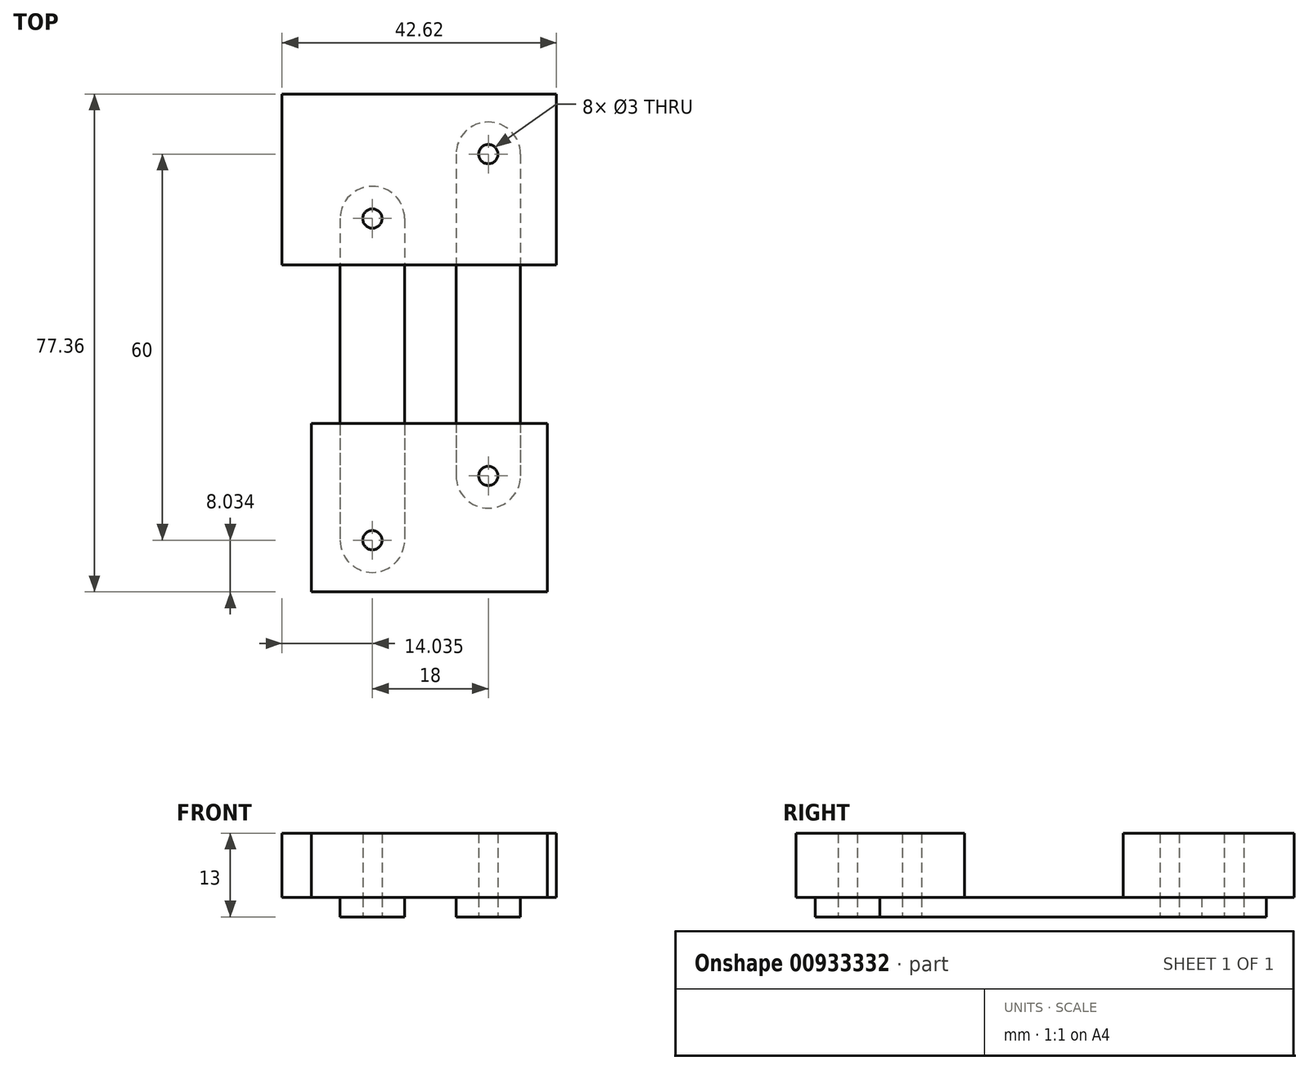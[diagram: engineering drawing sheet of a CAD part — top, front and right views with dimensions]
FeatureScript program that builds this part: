
annotation { "Feature Type Name" : "Feature", "Feature Type Description" : "" }
export const myFeature = defineFeature(function(context is Context, id is Id, definition is map)
    precondition{}
    {
        {
            var Q0;
            Q0=qCreatedBy(makeId("Top.planeOp"),FACE);
            var sketch = newSketch(context, id + "F0", { "sketchPlane" : qUnion([Q0])});
            skLineSegment(sketch, "E0.left", {"start": v(-39.37, 31.83) * mm, "end": v(-39.37, -18.17) * mm});
            skLineSegment(sketch, "E0.right", {"start": v(-29.37, 31.83) * mm, "end": v(-29.37, -18.17) * mm});
            skArc(sketch, "E1", {"start": v(-29.37, 31.83) * mm, "mid": v(-34.37, 36.83) * mm, "end": v(-39.37, 31.83) * mm});
            skArc(sketch, "E2", {"start": v(-39.37, -18.17) * mm, "mid": v(-34.37, -23.17) * mm, "end": v(-29.37, -18.17) * mm});
            skCircle(sketch, "E3", {"center": v(-34.37, 31.83) * mm, "radius": 1.5 * mm});
            skCircle(sketch, "E4", {"center": v(-34.37, -18.17) * mm, "radius": 1.5 * mm});
            skSolve(sketch);
        }
        {
            var Q0;
            Q0=makeQuery(id+"F0.imprint","IMPRINT",FACE,{"disambiguationData":[TD([[makeQuery(id+"F0.imprint","IMPRINT",EDGE,{"derivedFrom":sQuery(id+"F0.wireOp",EDGE,"E0.left")}),1.0]])]});
            extrude(context, id + "F1", {"entities" : qUnion([Q0]), "depth" : 3 * mm, "offsetDistance" : 25 * mm});
        }
        {
            var Q0;
            Q0=makeQuery(id+"F1.opExtrude","SWEPT_BODY",BODY,{"disambiguationData":[OSD([sQuery(id+"F0.wireOp",EDGE,"E0.left"),sQuery(id+"F0.wireOp",EDGE,"E0.right"),sQuery(id+"F0.wireOp",EDGE,"E1"),sQuery(id+"F0.wireOp",EDGE,"E2"),sQuery(id+"F0.wireOp",EDGE,"E3"),sQuery(id+"F0.wireOp",EDGE,"E4")])]});
            transform(context, id + "F2", {"entities" : qUnion([Q0]), "transformType" : TransformType.TRANSLATION_3D, "dx" : 18 * mm, "dy" : 10 * mm, "dz" : 0 * mm, "makeCopy" : true});
        }
        {
            var Q0;
            Q0=makeQuery(id+"F1.opExtrude","CAP_FACE",FACE,{"disambiguationData":[OSD([sQuery(id+"F0.wireOp",EDGE,"E0.left"),sQuery(id+"F0.wireOp",EDGE,"E0.right"),sQuery(id+"F0.wireOp",EDGE,"E1"),sQuery(id+"F0.wireOp",EDGE,"E2"),sQuery(id+"F0.wireOp",EDGE,"E3"),sQuery(id+"F0.wireOp",EDGE,"E4")])],"isStart":false});
            var sketch = newSketch(context, id + "F3", { "sketchPlane" : qUnion([Q0])});
            skLineSegment(sketch, "E5.bottom", {"start": v(-43.86, 0) * mm, "end": v(-7.2, 0) * mm});
            skLineSegment(sketch, "E5.top", {"start": v(-43.86, -26.2) * mm, "end": v(-7.2, -26.2) * mm});
            skLineSegment(sketch, "E5.left", {"start": v(-43.86, 0) * mm, "end": v(-43.86, -26.2) * mm});
            skLineSegment(sketch, "E5.right", {"start": v(-7.2, 0) * mm, "end": v(-7.2, -26.2) * mm});
            skCircle(sketch, "E6.0", {"center": v(-34.37, -18.17) * mm, "radius": 1.5 * mm});
            skCircle(sketch, "E7.0", {"center": v(-16.37, -8.17) * mm, "radius": 1.5 * mm});
            skSolve(sketch);
        }
        {
            var Q0;
            Q0=makeQuery(id+"F3.imprint","IMPRINT",FACE,{"disambiguationData":[TD([[makeQuery(id+"F3.imprint","IMPRINT",EDGE,{"derivedFrom":sQuery(id+"F3.wireOp",EDGE,"E5.top")}),1.0]])]});
            var Q1;
            Q1=makeQuery(id+"F3.imprint","IMPRINT",FACE,{"disambiguationData":[TD([[makeQuery(id+"F3.imprint","IMPRINT",EDGE,{"derivedFrom":sQuery(id+"F3.wireOp",EDGE,"E6.0")}),-1.0]])]});
            extrude(context, id + "F4", {"entities" : qUnion([Q0, Q1]), "depth" : 10 * mm, "offsetDistance" : 25 * mm});
        }
        {
            var Q0;
            Q0=makeQuery(id+"F1.opExtrude","CAP_FACE",FACE,{"disambiguationData":[OSD([sQuery(id+"F0.wireOp",EDGE,"E0.left"),sQuery(id+"F0.wireOp",EDGE,"E0.right"),sQuery(id+"F0.wireOp",EDGE,"E1"),sQuery(id+"F0.wireOp",EDGE,"E2"),sQuery(id+"F0.wireOp",EDGE,"E3"),sQuery(id+"F0.wireOp",EDGE,"E4")])],"isStart":false});
            var sketch = newSketch(context, id + "F5", { "sketchPlane" : qUnion([Q0])});
            skLineSegment(sketch, "E8.bottom", {"start": v(-48.4, 51.16) * mm, "end": v(-5.8, 51.16) * mm});
            skLineSegment(sketch, "E8.top", {"start": v(-48.4, 24.65) * mm, "end": v(-5.8, 24.65) * mm});
            skLineSegment(sketch, "E8.left", {"start": v(-48.4, 51.16) * mm, "end": v(-48.4, 24.65) * mm});
            skLineSegment(sketch, "E8.right", {"start": v(-5.8, 51.16) * mm, "end": v(-5.8, 24.65) * mm});
            skCircle(sketch, "E9.0", {"center": v(-34.37, 31.83) * mm, "radius": 1.5 * mm});
            skCircle(sketch, "E10.0", {"center": v(-16.37, 41.83) * mm, "radius": 1.5 * mm});
            skSolve(sketch);
        }
        {
            var Q0;
            Q0=makeQuery(id+"F5.imprint","IMPRINT",FACE,{"disambiguationData":[TD([[makeQuery(id+"F5.imprint","IMPRINT",EDGE,{"derivedFrom":sQuery(id+"F5.wireOp",EDGE,"E8.bottom")}),-1.0]])]});
            var Q1;
            Q1=makeQuery(id+"F5.imprint","IMPRINT",FACE,{"disambiguationData":[TD([[makeQuery(id+"F5.imprint","IMPRINT",EDGE,{"derivedFrom":sQuery(id+"F5.wireOp",EDGE,"E9.0")}),-1.0]])]});
            extrude(context, id + "F6", {"entities" : qUnion([Q0, Q1]), "depth" : 10 * mm, "offsetDistance" : 25 * mm});
        }
    });
